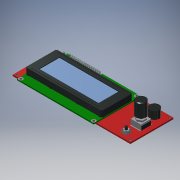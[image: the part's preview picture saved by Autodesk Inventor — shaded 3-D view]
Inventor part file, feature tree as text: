
AUTODESK INVENTOR PART (.ipt)
format: ipt  version: 2018 (Build 220112000, 112)  size: 649,728 bytes
history: native  units: mm
features: chamfer x1
ambient origin geometry x8: Origin, YZ Plane, XZ Plane, XY Plane, X Axis, Y Axis, Z Axis, Center Point
bodies: Solid1 (feature_tree)
feature tree (1):
  chamfer  "Chamfer6"  [1 undecoded]
note: 1 required parameter value undecoded (feature->parameter linkage not recoverable at this tier; creation-order binding heuristic only, values carry confidence <= 0.55)
